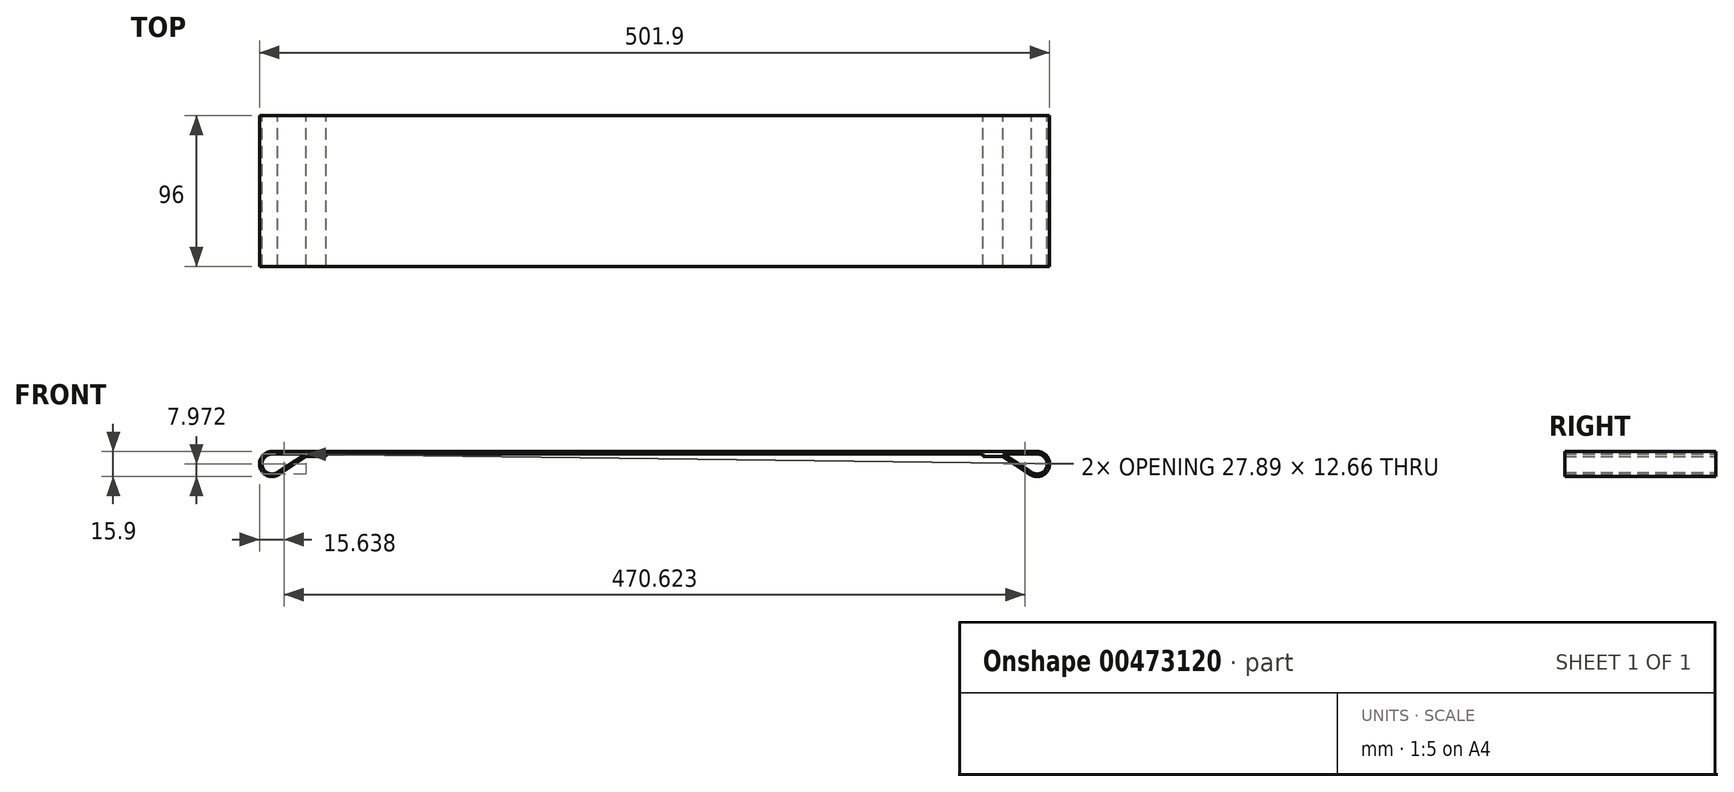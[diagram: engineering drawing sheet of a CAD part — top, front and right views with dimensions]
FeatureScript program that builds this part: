
annotation { "Feature Type Name" : "Feature", "Feature Type Description" : "" }
export const myFeature = defineFeature(function(context is Context, id is Id, definition is map)
    precondition{}
    {
        {
            var Q0;
            Q0=qCreatedBy(makeId("Top.planeOp"),FACE);
            var sketch = newSketch(context, id + "F0", { "sketchPlane" : qUnion([Q0])});
            skLineSegment(sketch, "E0.bottom", {"start": v(-251.5, 48) * mm, "end": v(251.5, 48) * mm});
            skLineSegment(sketch, "E0.top", {"start": v(-251.5, -48) * mm, "end": v(251.5, -48) * mm});
            skLineSegment(sketch, "E0.left", {"start": v(-251.5, 48) * mm, "end": v(-251.5, -48) * mm});
            skLineSegment(sketch, "E0.right", {"start": v(251.5, 48) * mm, "end": v(251.5, -48) * mm});
            skPoint(sketch, "E0.middle", {"position": v(0, 0) * mm});
            skSolve(sketch);
        }
        {
            var Q0;
            Q0=qCreatedBy(makeId("Front.planeOp"),FACE);
            var sketch = newSketch(context, id + "F1", { "sketchPlane" : qUnion([Q0])});
            skCircle(sketch, "E1", {"center": v(-243, 0) * mm, "radius": 6.35 * mm});
            skLineSegment(sketch, "E2", {"start": v(-239.5, -5.3) * mm, "end": v(-221.37, 6.35) * mm});
            skLineSegment(sketch, "E3", {"start": v(-221.37, 6.35) * mm, "end": v(-208.5, 6.35) * mm});
            skLineSegment(sketch, "E4", {"start": v(-208.5, 6.35) * mm, "end": v(-208.5, 4.75) * mm});
            skLineSegment(sketch, "E5", {"start": v(-208.5, 4.75) * mm, "end": v(-221.37, 4.75) * mm});
            skLineSegment(sketch, "E6", {"start": v(-221.37, 4.75) * mm, "end": v(-239.5, -7.22) * mm});
            skCircle(sketch, "E7", {"center": v(-243, 0) * mm, "radius": 7.95 * mm});
            skLineSegment(sketch, "E8", {"start": v(-243, 7.95) * mm, "end": v(0, 7.95) * mm});
            skLineSegment(sketch, "E9", {"start": v(0, 7.95) * mm, "end": v(0, 6.35) * mm});
            skLineSegment(sketch, "E10", {"start": v(-243, 6.35) * mm, "end": v(0, 6.35) * mm});
            skSolve(sketch);
        }
        {
            var Q0;
            Q0 = qSketchRegion(id + "F1", true);
            extrude(context, id + "F2", {"entities" : qUnion([Q0]), "depth" : 48 * mm, "offsetDistance" : 25 * mm, "hasSecondDirection" : true, "secondDirectionOppositeDirection" : true, "secondDirectionDepth" : 48 * mm});
        }
        {
            var Q0;
            Q0=makeQuery(id+"F2.opExtrude","SWEPT_BODY",BODY,{"disambiguationData":[OSD([sQuery(id+"F1.wireOp",EDGE,"E1"),sQuery(id+"F1.wireOp",EDGE,"E2"),sQuery(id+"F1.wireOp",EDGE,"E4"),sQuery(id+"F1.wireOp",EDGE,"E5"),sQuery(id+"F1.wireOp",EDGE,"E6"),sQuery(id+"F1.wireOp",EDGE,"E7"),sQuery(id+"F1.wireOp",EDGE,"E8"),sQuery(id+"F1.wireOp",EDGE,"E9"),sQuery(id+"F1.wireOp",EDGE,"E10")])]});
            var Q1;
            Q1=qCreatedBy(makeId("Right.planeOp"),FACE);
            mirror(context, id + "F3", {"operationType" : NewBodyOperationType.ADD, "entities" : qUnion([Q0]), "mirrorPlane" : qUnion([Q1])});
        }
    });
